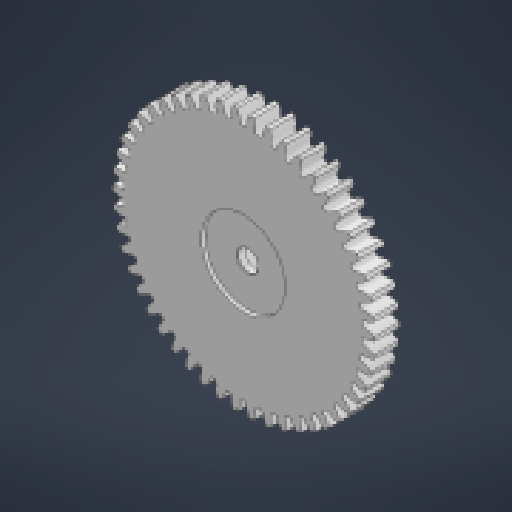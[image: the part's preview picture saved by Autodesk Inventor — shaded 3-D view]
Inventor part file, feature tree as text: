
AUTODESK INVENTOR PART (.ipt)
format: ipt  version: 2024.1 (Build 281209000, 209)  size: 464,384 bytes
history: native  units: in
note: dims shown in document units (in); Inventor stores cm internally (conversion verified against a paired STEP export)
features: extrude x5, sketch x2, pattern_circular x1, chamfer x1
ambient origin geometry x8: Origin, YZ Plane, XZ Plane, XY Plane, X Axis, Y Axis, Z Axis, Center Point
bodies: Solid1 (feature_tree)
feature tree (9):
  extrude  "Extrusion1"  TaperAngle=0.0deg  [1 undecoded]
  extrude  "Extrusion2"  Depth=0.125in TaperAngle=360.0deg
  pattern_circular  "Circular Pattern1"  [2 undecoded]
  sketch  "Sketch2"  dims[d0=0.15in d1=0.0in]
  extrude  "Extrusion3"  Depth=0.125in
  extrude  "Extrusion4"  Depth=0.125in TaperAngle=0.0deg
  extrude  "Extrusion5"  TaperAngle=0.0deg  [1 undecoded]
  chamfer  "Chamfer1"  Distance=0.5in
  sketch  "Sketch3"  dims[d2=0.0in d3=0.0in d4=19.685in d5=360.0deg d7=0.2047in d8=0.122in d9=0.0787in d10=0.0in d11=0.0in d12=0.0in d13=0.5in d14=0.025in d15=0.0in d16=0.005in d17=0.125in d18=45.0deg]
note: 4 required parameter values undecoded (feature->parameter linkage not recoverable at this tier; creation-order binding heuristic only, values carry confidence <= 0.55)
